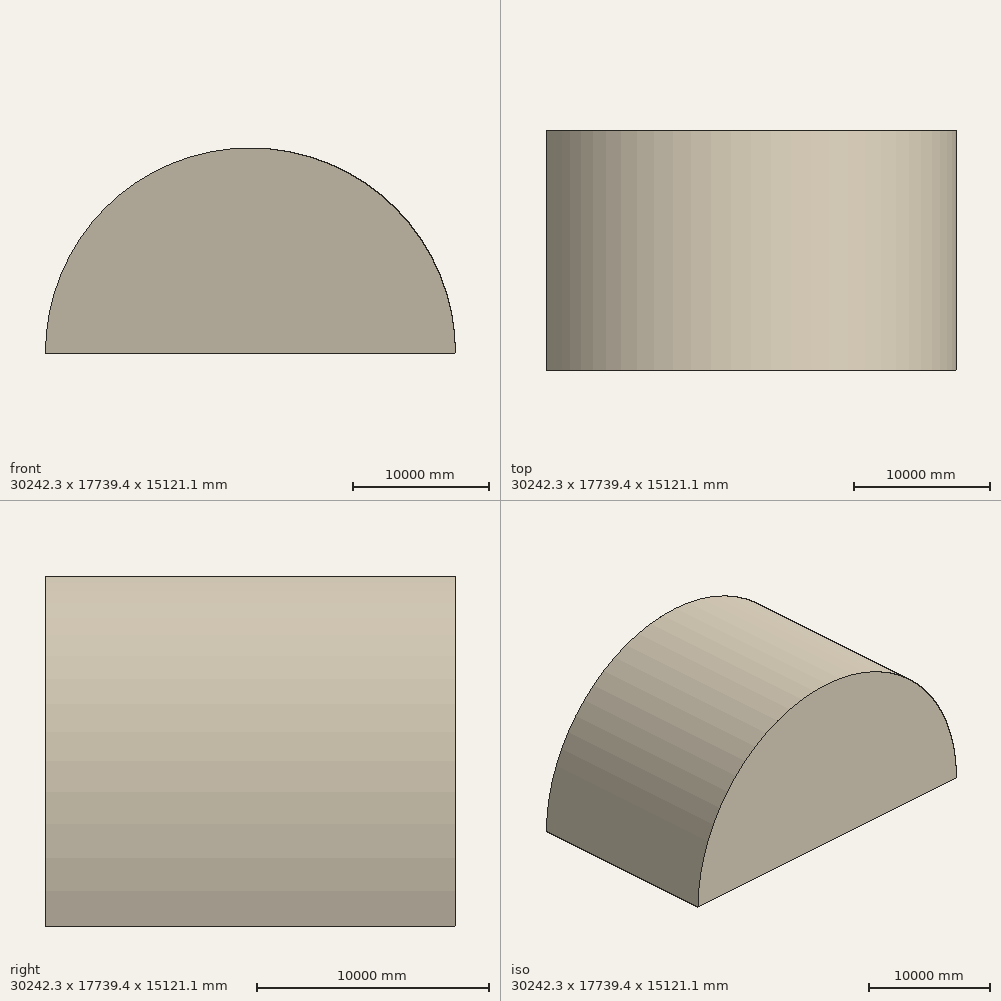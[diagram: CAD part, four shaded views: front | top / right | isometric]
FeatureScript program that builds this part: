
annotation { "Feature Type Name" : "Feature", "Feature Type Description" : "" }
export const myFeature = defineFeature(function(context is Context, id is Id, definition is map)
    precondition{}
    {
        {
            var Q0;
            Q0=qCreatedBy(makeId("Front.planeOp"),FACE);
            var sketch = newSketch(context, id + "F0", { "sketchPlane" : qUnion([Q0])});
            skArc(sketch, "E0", {"start": v(15121.13, 0) * mm, "mid": v(0, 15121.13) * mm, "end": v(-15121.13, 0) * mm});
            skLineSegment(sketch, "E1", {"start": v(0, 0) * mm, "end": v(15121.13, 0) * mm});
            skLineSegment(sketch, "E2", {"start": v(0, 0) * mm, "end": v(-15121.13, 0) * mm});
            skSolve(sketch);
        }
        {
            var Q0;
            {var subQ0=sQuery(id+"F0.wireOp",EDGE,"E1");Q0=makeQuery(id+"F0.imprint","IMPRINT",FACE,{"disambiguationData":[TD([[makeQuery(id+"F0.imprint","IMPRINT",EDGE,{"derivedFrom":subQ0}),1.0]])]});}
            extrude(context, id + "F1", {"entities" : qUnion([Q0]), "depth" : 17739.36 * mm, "offsetDistance" : 25.4 * mm});
        }
    });
